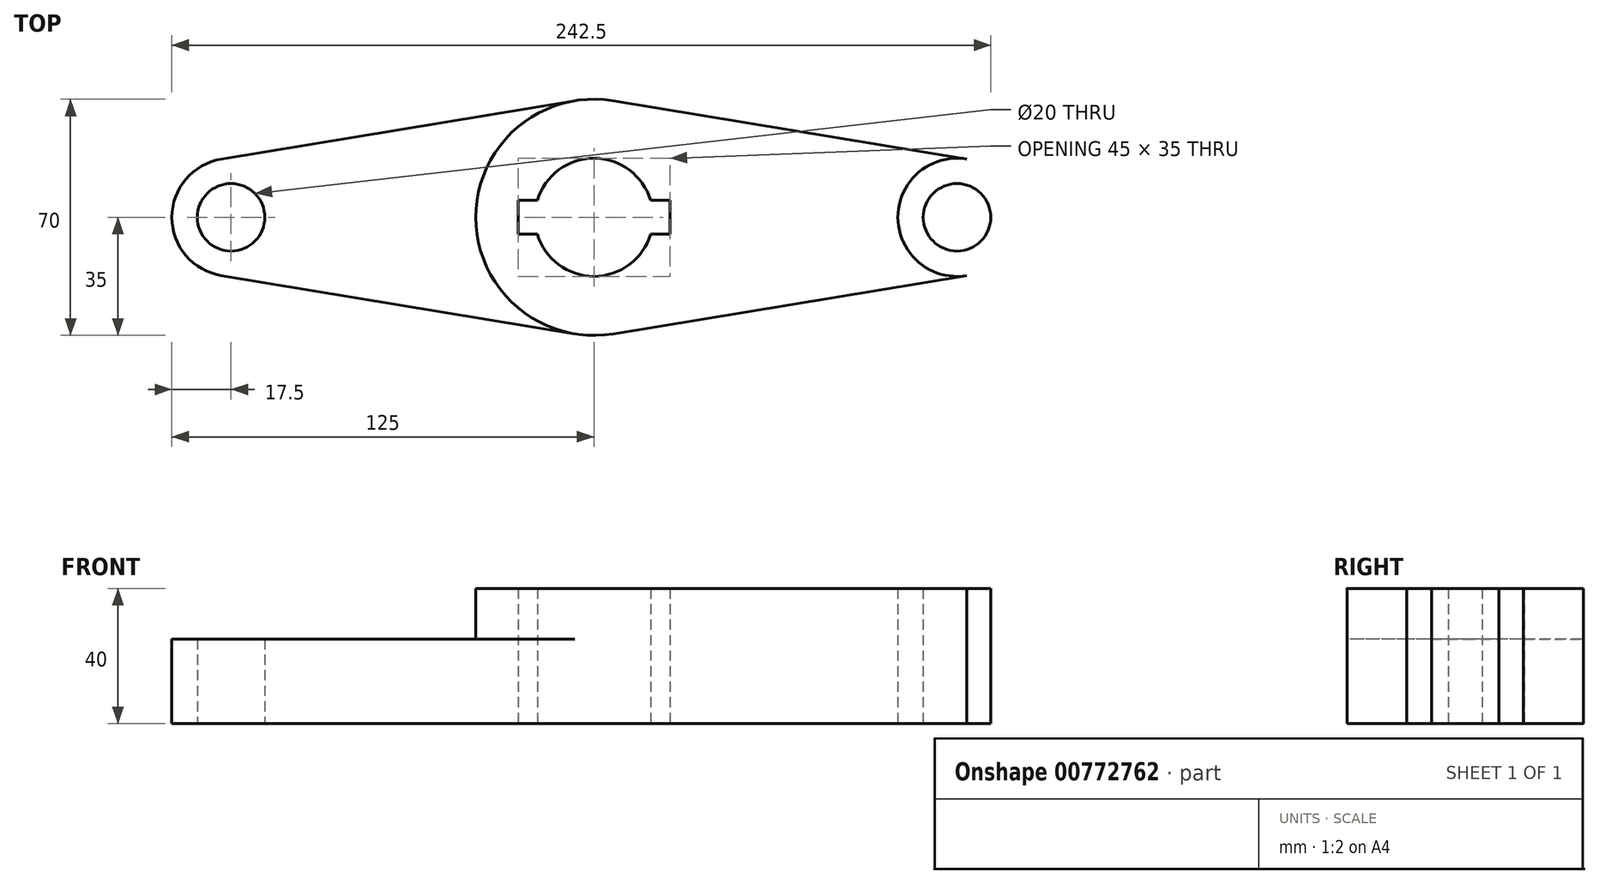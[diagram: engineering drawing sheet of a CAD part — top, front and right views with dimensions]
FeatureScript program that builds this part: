
annotation { "Feature Type Name" : "Feature", "Feature Type Description" : "" }
export const myFeature = defineFeature(function(context is Context, id is Id, definition is map)
    precondition{}
    {
        {
            var Q0;
            Q0=qCreatedBy(makeId("Top.planeOp"),FACE);
            var sketch = newSketch(context, id + "F0", { "sketchPlane" : qUnion([Q0])});
            skLineSegment(sketch, "E0", {"start": v(0, 0) * mm, "end": v(0, 76.64) * mm, "construction": true});
            skCircle(sketch, "E1", {"center": v(0, 0) * mm, "radius": 35 * mm});
            skCircle(sketch, "E2", {"center": v(0, 0) * mm, "radius": 17.5 * mm});
            skLineSegment(sketch, "E3.bottom", {"start": v(22.5, -5) * mm, "end": v(-22.5, -5) * mm});
            skLineSegment(sketch, "E3.top", {"start": v(22.5, 5) * mm, "end": v(-22.5, 5) * mm});
            skLineSegment(sketch, "E3.left", {"start": v(22.5, -5) * mm, "end": v(22.5, 5) * mm});
            skLineSegment(sketch, "E3.right", {"start": v(-22.5, -5) * mm, "end": v(-22.5, 5) * mm});
            skCircle(sketch, "E4", {"center": v(-107.5, 0) * mm, "radius": 17.5 * mm});
            skCircle(sketch, "E5", {"center": v(-107.5, 0) * mm, "radius": 10 * mm});
            skLineSegment(sketch, "E6", {"start": v(-110.35, 17.27) * mm, "end": v(-5.7, 34.53) * mm});
            skLineSegment(sketch, "E7", {"start": v(-110.35, -17.27) * mm, "end": v(-5.7, -34.53) * mm});
            skLineSegment(sketch, "E8.MirrorCS", {"start": v(110.35, 17.27) * mm, "end": v(5.7, 34.53) * mm});
            skLineSegment(sketch, "E9.MirrorCS", {"start": v(110.35, -17.27) * mm, "end": v(5.7, -34.53) * mm});
            skCircle(sketch, "E10.MirrorC", {"center": v(107.5, 0) * mm, "radius": 17.5 * mm});
            skCircle(sketch, "E11.MirrorC", {"center": v(107.5, 0) * mm, "radius": 10 * mm});
            skSolve(sketch);
        }
        {
            var Q0;
            {var subQ4=sQuery(id+"F0.wireOp",EDGE,"E3.left");Q0=makeQuery(id+"F0.imprint","IMPRINT",FACE,{"disambiguationData":[TD([[makeQuery(id+"F0.imprint","IMPRINT",EDGE,{"derivedFrom":subQ4}),-1.0]])]});}
            var Q1;
            {var subQ0=sQuery(id+"F0.wireOp",EDGE,"E8.MirrorCS");Q1=makeQuery(id+"F0.imprint","IMPRINT",FACE,{"disambiguationData":[TD([[makeQuery(id+"F0.imprint","IMPRINT",EDGE,{"derivedFrom":subQ0}),1.0]])]});}
            var Q2;
            Q2=makeQuery(id+"F0.imprint","IMPRINT",FACE,{"disambiguationData":[TD([[makeQuery(id+"F0.imprint","IMPRINT",EDGE,{"derivedFrom":sQuery(id+"F0.wireOp",EDGE,"E11.MirrorC")}),1.0]])]});
            extrude(context, id + "F1", {"entities" : qUnion([Q0, Q1, Q2]), "depth" : 40 * mm, "offsetDistance" : 25 * mm});
        }
        {
            var Q0;
            {var subQ0=sQuery(id+"F0.wireOp",EDGE,"E6");Q0=makeQuery(id+"F0.imprint","IMPRINT",FACE,{"disambiguationData":[TD([[makeQuery(id+"F0.imprint","IMPRINT",EDGE,{"derivedFrom":subQ0}),-1.0]])]});}
            var Q1;
            Q1=makeQuery(id+"F0.imprint","IMPRINT",FACE,{"disambiguationData":[TD([[makeQuery(id+"F0.imprint","IMPRINT",EDGE,{"derivedFrom":sQuery(id+"F0.wireOp",EDGE,"E5")}),-1.0]])]});
            extrude(context, id + "F2", {"entities" : qUnion([Q0, Q1]), "operationType" : NewBodyOperationType.ADD, "depth" : 25 * mm, "offsetDistance" : 25 * mm});
        }
    });
